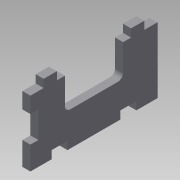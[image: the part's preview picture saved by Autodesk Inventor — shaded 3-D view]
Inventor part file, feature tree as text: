
AUTODESK INVENTOR PART (.ipt)
format: ipt  version: 2013 (Build 170138000, 138)  size: 115,712 bytes
history: native  units: mm
features: extrude x1, sketch x1
ambient origin geometry x8: Origin, YZ Plane, XZ Plane, XY Plane, X Axis, Y Axis, Z Axis, Center Point
bodies: Solid1 (feature_tree)
feature tree (2):
  extrude  "Extrusion1"  Depth=3.0mm
  sketch  "Sketch1"  dims[d4=19.0mm d6=3.0mm d7=3.0mm d8=10.0mm d18=3.0mm d19=0.0mm d70=5.0mm d71=3.0mm d72=5.0mm d74=2.0mm d75=5.0mm d76=5.0mm d78=48.0mm d79=13.0mm d80=13.0mm d83=3.0mm d86=6.0mm d88=8.0mm d89=6.0mm d90=6.0mm d91=8.0mm d92=3.0mm d93=3.0mm]
